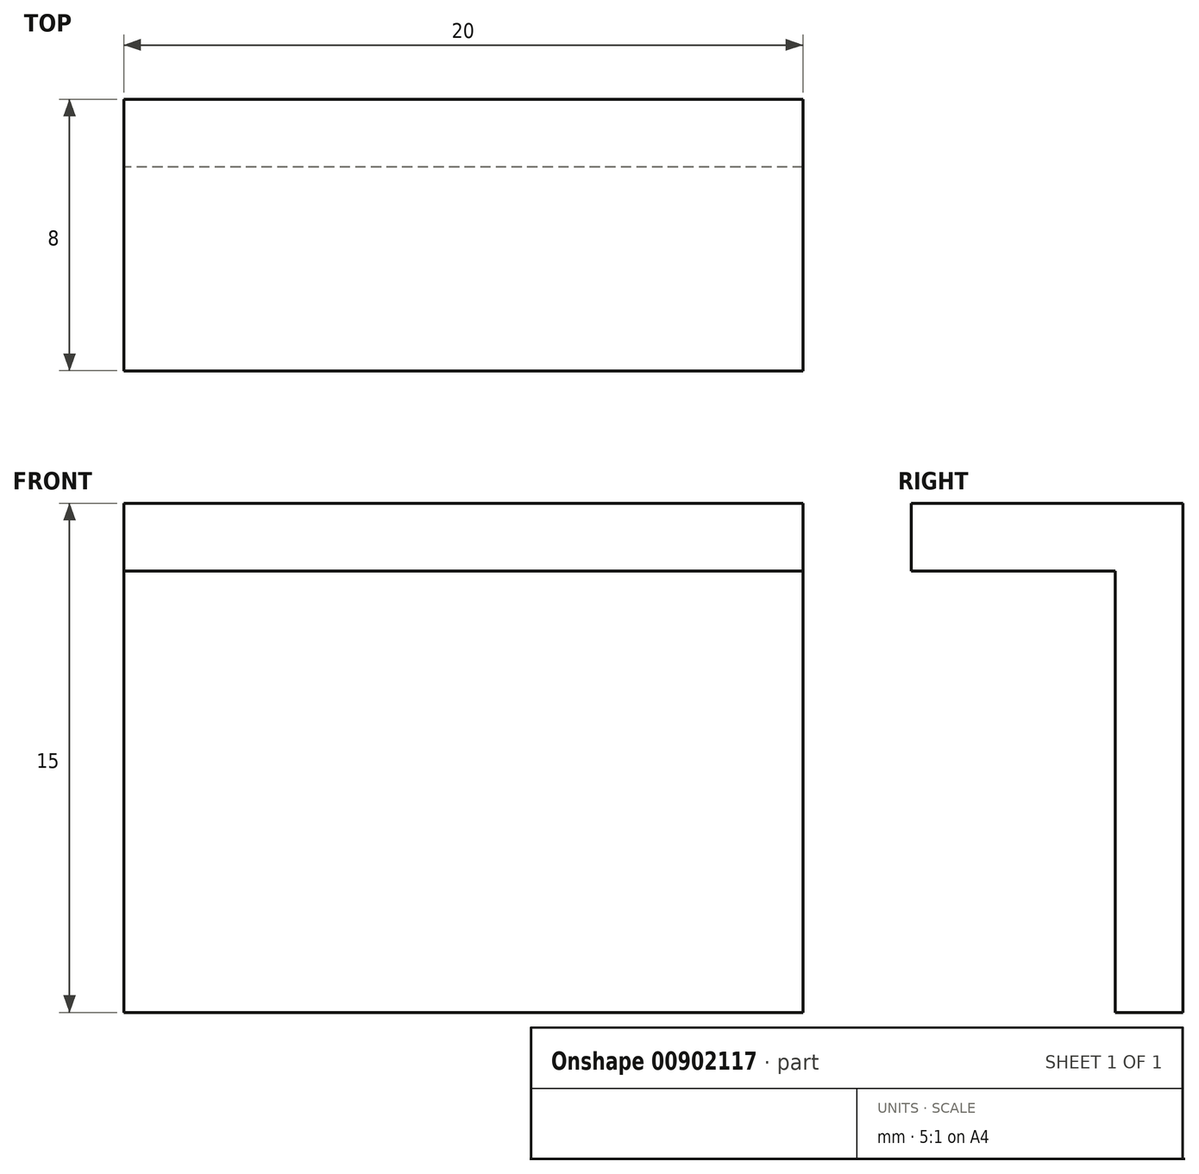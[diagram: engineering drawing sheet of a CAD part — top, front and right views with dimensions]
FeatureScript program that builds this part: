
annotation { "Feature Type Name" : "Feature", "Feature Type Description" : "" }
export const myFeature = defineFeature(function(context is Context, id is Id, definition is map)
    precondition{}
    {
        {
            var Q0;
            Q0=qCreatedBy(makeId("Right.planeOp"),FACE);
            var sketch = newSketch(context, id + "F0", { "sketchPlane" : qUnion([Q0])});
            skLineSegment(sketch, "E0.left", {"start": v(7.2, -1) * mm, "end": v(7.2, 1) * mm});
            skPoint(sketch, "E0.middle", {"position": v(0, 0) * mm});
            skLineSegment(sketch, "E1", {"start": v(7.2, 0) * mm, "end": v(5.2, 0) * mm});
            skLineSegment(sketch, "E2", {"start": v(5.2, -1) * mm, "end": v(5.2, -14) * mm});
            skLineSegment(sketch, "E3", {"start": v(7.2, -1) * mm, "end": v(7.2, -14) * mm});
            skLineSegment(sketch, "E4", {"start": v(5.2, -14) * mm, "end": v(7.2, -14) * mm});
            skLineSegment(sketch, "E5", {"start": v(7.2, 1) * mm, "end": v(-0.8, 1) * mm});
            skLineSegment(sketch, "E6", {"start": v(5.2, -1) * mm, "end": v(-0.8, -1) * mm});
            skLineSegment(sketch, "E7", {"start": v(-0.8, -1) * mm, "end": v(-0.8, 1) * mm});
            skSolve(sketch);
        }
        {
            var Q0;
            Q0=makeQuery(id+"F0.imprint","IMPRINT",FACE,{"disambiguationData":[TD([[makeQuery(id+"F0.imprint","IMPRINT",EDGE,{"derivedFrom":sQuery(id+"F0.wireOp",EDGE,"E2")}),1.0]])]});
            extrude(context, id + "F1", {"entities" : qUnion([Q0]), "depth" : 20 * mm, "offsetDistance" : 25 * mm});
        }
    });
